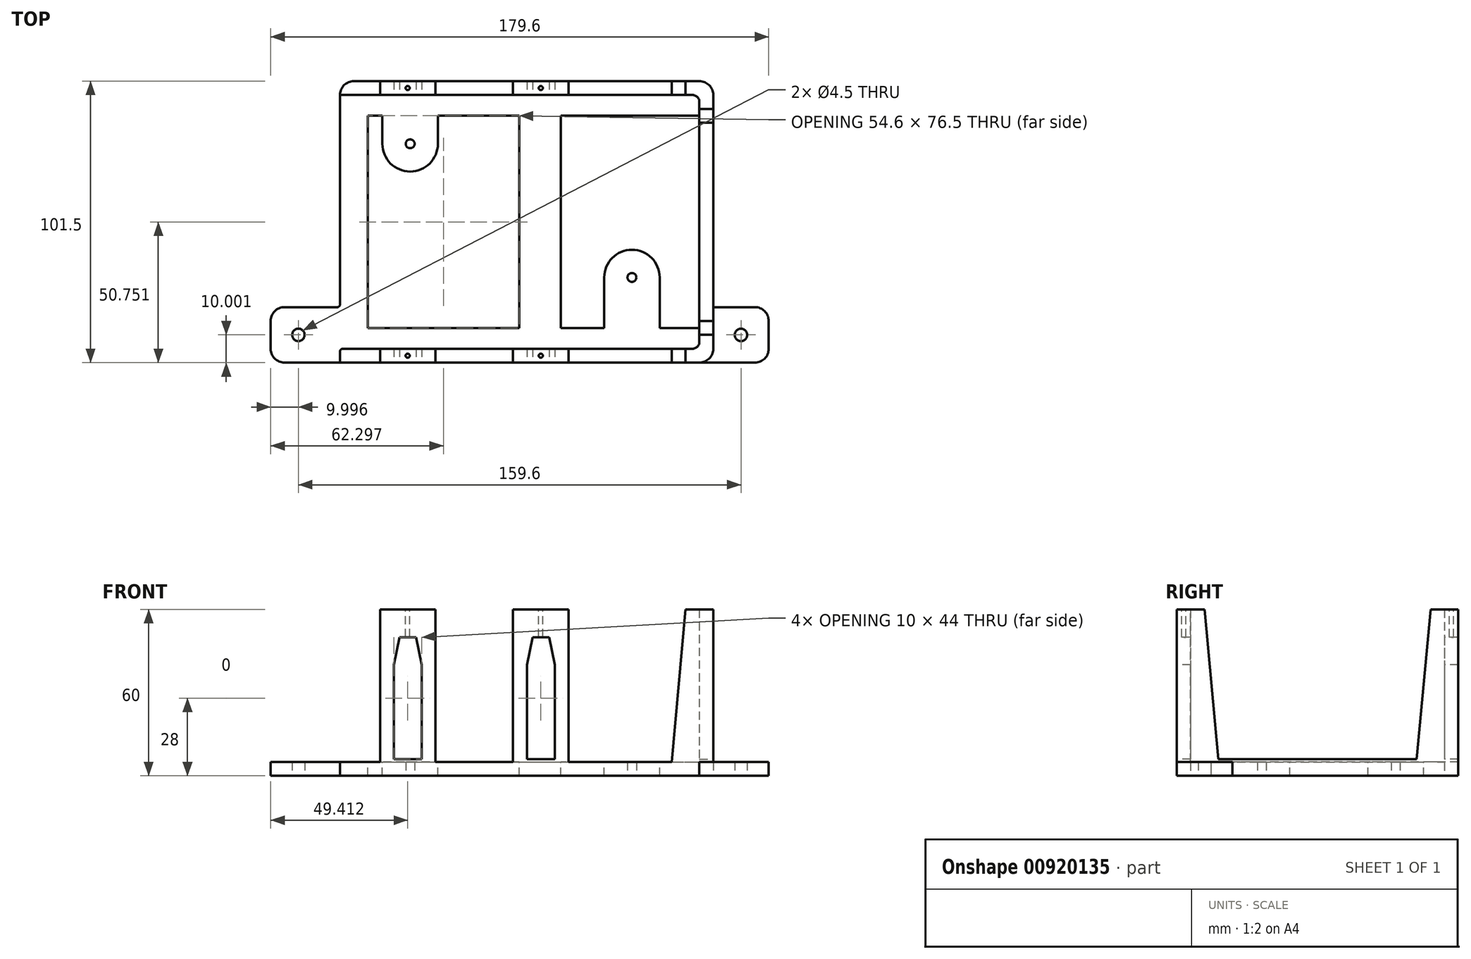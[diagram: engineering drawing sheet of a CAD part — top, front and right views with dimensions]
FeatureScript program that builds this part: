
annotation { "Feature Type Name" : "Feature", "Feature Type Description" : "" }
export const myFeature = defineFeature(function(context is Context, id is Id, definition is map)
    precondition{}
    {
        {
            var Q0;
            Q0=qCreatedBy(makeId("Top.planeOp"),FACE);
            var sketch = newSketch(context, id + "F0", { "sketchPlane" : qUnion([Q0])});
            skLineSegment(sketch, "E0.bottom", {"start": v(-74.7, 33.21) * mm, "end": v(26.9, 33.21) * mm, "construction": true});
            skLineSegment(sketch, "E0.top", {"start": v(-74.7, -20.09) * mm, "end": v(26.9, -20.09) * mm, "construction": true});
            skLineSegment(sketch, "E0.left", {"start": v(-74.7, 33.21) * mm, "end": v(-74.7, -20.09) * mm, "construction": true});
            skLineSegment(sketch, "E0.right", {"start": v(26.9, 33.21) * mm, "end": v(26.9, -20.09) * mm, "construction": true});
            skCircle(sketch, "E1", {"center": v(-60.7, -17.59) * mm, "radius": 1.6 * mm, "construction": true});
            skCircle(sketch, "E2", {"center": v(-59.4, 30.61) * mm, "radius": 1.6 * mm});
            skCircle(sketch, "E3", {"center": v(15.5, 30.61) * mm, "radius": 1.6 * mm, "construction": true});
            skCircle(sketch, "E4", {"center": v(20.58, -17.59) * mm, "radius": 1.6 * mm});
            skCircle(sketch, "E5", {"center": v(-8.6, -12.49) * mm, "radius": 1.6 * mm, "construction": true});
            skCircle(sketch, "E6", {"center": v(-8.6, 15.41) * mm, "radius": 1.6 * mm, "construction": true});
            skLineSegment(sketch, "E7.bottom", {"start": v(-79.7, 53.21) * mm, "end": v(44.9, 53.21) * mm});
            skLineSegment(sketch, "E7.top", {"start": v(-84.7, -48.29) * mm, "end": v(44.9, -48.29) * mm});
            skLineSegment(sketch, "E7.left", {"start": v(-50.13, 53.21) * mm, "end": v(-50.13, -48.29) * mm, "construction": true});
            skLineSegment(sketch, "E7.right", {"start": v(49.9, 48.21) * mm, "end": v(49.9, -43.29) * mm});
            skLineSegment(sketch, "E8.0", {"start": v(-83.7, -43.29) * mm, "end": v(42.4, -43.29) * mm});
            skLineSegment(sketch, "E8.1", {"start": v(44.9, 45.71) * mm, "end": v(44.9, -40.79) * mm});
            skLineSegment(sketch, "E8.2", {"start": v(-84.7, 48.21) * mm, "end": v(42.4, 48.21) * mm});
            skLineSegment(sketch, "E9", {"start": v(-84.7, 48.21) * mm, "end": v(-84.7, -27.29) * mm});
            skLineSegment(sketch, "E10", {"start": v(-104.7, -28.29) * mm, "end": v(-85.7, -28.29) * mm});
            skLineSegment(sketch, "E11", {"start": v(-109.7, -33.29) * mm, "end": v(-109.7, -43.29) * mm});
            skLineSegment(sketch, "E12", {"start": v(-104.7, -48.29) * mm, "end": v(-84.7, -48.29) * mm});
            skLineSegment(sketch, "E13", {"start": v(44.9, -48.29) * mm, "end": v(64.9, -48.29) * mm});
            skLineSegment(sketch, "E14", {"start": v(69.9, -43.29) * mm, "end": v(69.9, -33.29) * mm});
            skLineSegment(sketch, "E15.trimOffspring", {"start": v(49.9, -28.29) * mm, "end": v(64.9, -28.29) * mm});
            skLineSegment(sketch, "E16.trimOffspring", {"start": v(-84.7, -44.29) * mm, "end": v(-84.7, -48.29) * mm});
            skCircle(sketch, "E17", {"center": v(-99.7, -38.29) * mm, "radius": 2.25 * mm});
            skCircle(sketch, "E18", {"center": v(59.9, -38.29) * mm, "radius": 2.25 * mm});
            skPoint(sketch, "E19.visualSharp", {"position": v(44.9, 48.21) * mm});
            skArc(sketch, "E19.filletArc", {"start": v(44.9, 45.71) * mm, "mid": v(44.16, 47.48) * mm, "end": v(42.4, 48.21) * mm});
            skPoint(sketch, "E20.visualSharp", {"position": v(49.9, 53.21) * mm});
            skArc(sketch, "E20.filletArc", {"start": v(49.9, 48.21) * mm, "mid": v(48.43, 51.75) * mm, "end": v(44.9, 53.21) * mm});
            skPoint(sketch, "E21.visualSharp", {"position": v(44.9, -43.29) * mm});
            skArc(sketch, "E21.filletArc", {"start": v(42.4, -43.29) * mm, "mid": v(44.16, -42.56) * mm, "end": v(44.9, -40.79) * mm});
            skPoint(sketch, "E22.visualSharp", {"position": v(-109.7, -48.29) * mm});
            skArc(sketch, "E22.filletArc", {"start": v(-109.7, -43.29) * mm, "mid": v(-108.24, -46.82) * mm, "end": v(-104.7, -48.29) * mm});
            skPoint(sketch, "E23.visualSharp", {"position": v(-109.7, -28.29) * mm});
            skArc(sketch, "E23.filletArc", {"start": v(-104.7, -28.29) * mm, "mid": v(-108.24, -29.75) * mm, "end": v(-109.7, -33.29) * mm});
            skPoint(sketch, "E24.visualSharp", {"position": v(69.9, -28.29) * mm});
            skArc(sketch, "E24.filletArc", {"start": v(69.9, -33.29) * mm, "mid": v(68.43, -29.75) * mm, "end": v(64.9, -28.29) * mm});
            skPoint(sketch, "E25.visualSharp", {"position": v(69.9, -48.29) * mm});
            skArc(sketch, "E25.filletArc", {"start": v(64.9, -48.29) * mm, "mid": v(68.43, -46.82) * mm, "end": v(69.9, -43.29) * mm});
            skPoint(sketch, "E26.visualSharp", {"position": v(-84.7, 53.21) * mm});
            skArc(sketch, "E26.filletArc", {"start": v(-79.7, 53.21) * mm, "mid": v(-83.24, 51.75) * mm, "end": v(-84.7, 48.21) * mm});
            skPoint(sketch, "E27.visualSharp", {"position": v(-84.7, -28.29) * mm});
            skArc(sketch, "E27.filletArc", {"start": v(-85.7, -28.29) * mm, "mid": v(-85, -28) * mm, "end": v(-84.7, -27.29) * mm});
            skPoint(sketch, "E28.visualSharp", {"position": v(-84.7, -43.29) * mm});
            skArc(sketch, "E28.filletArc", {"start": v(-83.7, -43.29) * mm, "mid": v(-84.41, -43.58) * mm, "end": v(-84.7, -44.29) * mm});
            skPoint(sketch, "E29.visualSharp", {"position": v(49.9, -48.29) * mm});
            skArc(sketch, "E29.filletArc", {"start": v(44.9, -48.29) * mm, "mid": v(48.43, -46.82) * mm, "end": v(49.9, -43.29) * mm});
            skSolve(sketch);
        }
        {
            var Q0;
            Q0=makeQuery(id+"F0.imprint","IMPRINT",FACE,{"disambiguationData":[TD([[makeQuery(id+"F0.imprint","IMPRINT",EDGE,{"derivedFrom":sQuery(id+"F0.wireOp",EDGE,"E2")}),-1.0]])]});
            var Q1;
            {var subQ0=sQuery(id+"F0.wireOp",EDGE,"E13");Q1=makeQuery(id+"F0.imprint","IMPRINT",FACE,{"disambiguationData":[TD([[makeQuery(id+"F0.imprint","IMPRINT",EDGE,{"derivedFrom":subQ0}),1.0]])]});}
            extrude(context, id + "F1", {"entities" : qUnion([Q0, Q1]), "depth" : 5 * mm, "offsetDistance" : 25 * mm});
        }
        {
            var Q0;
            Q0=makeQuery(id+"F0.imprint","IMPRINT",FACE,{"disambiguationData":[TD([[makeQuery(id+"F0.imprint","IMPRINT",EDGE,{"derivedFrom":sQuery(id+"F0.wireOp",EDGE,"E7.bottom")}),-1.0]])]});
            extrude(context, id + "F2", {"entities" : qUnion([Q0]), "depth" : 60 * mm, "offsetDistance" : 25 * mm});
        }
        {
            var Q0;
            Q0=makeQuery(id+"F2.opExtrude","CAP_FACE",FACE,{"disambiguationData":[OSD([sQuery(id+"F0.wireOp",EDGE,"E7.bottom"),sQuery(id+"F0.wireOp",EDGE,"E7.top"),sQuery(id+"F0.wireOp",EDGE,"E7.right"),sQuery(id+"F0.wireOp",EDGE,"E8.0"),sQuery(id+"F0.wireOp",EDGE,"E8.1"),sQuery(id+"F0.wireOp",EDGE,"E8.2"),sQuery(id+"F0.wireOp",EDGE,"E16.trimOffspring"),sQuery(id+"F0.wireOp",EDGE,"E19.filletArc"),sQuery(id+"F0.wireOp",EDGE,"E20.filletArc"),sQuery(id+"F0.wireOp",EDGE,"E21.filletArc"),sQuery(id+"F0.wireOp",EDGE,"E26.filletArc"),sQuery(id+"F0.wireOp",EDGE,"E28.filletArc"),sQuery(id+"F0.wireOp",EDGE,"E29.filletArc")])],"isStart":false});
            var sketch = newSketch(context, id + "F3", { "sketchPlane" : qUnion([Q0])});
            skLineSegment(sketch, "E30", {"start": v(-88.25, 50.71) * mm, "end": v(116.83, 50.71) * mm, "construction": true});
            skLineSegment(sketch, "E31", {"start": v(-113.69, -45.79) * mm, "end": v(146.47, -45.79) * mm, "construction": true});
            skLineSegment(sketch, "E32.0", {"start": v(-83.7, -43.29) * mm, "end": v(42.4, -43.29) * mm});
            skLineSegment(sketch, "E33.0", {"start": v(-84.7, -48.29) * mm, "end": v(44.9, -48.29) * mm});
            skLineSegment(sketch, "E34.0", {"start": v(-84.7, 48.21) * mm, "end": v(42.4, 48.21) * mm});
            skLineSegment(sketch, "E35.0", {"start": v(-79.7, 53.21) * mm, "end": v(44.9, 53.21) * mm});
            skCircle(sketch, "E36", {"center": v(-60.29, 50.71) * mm, "radius": 0.75 * mm});
            skLineSegment(sketch, "E37", {"start": v(-60.29, 50.71) * mm, "end": v(-60.29, -65.98) * mm, "construction": true});
            skCircle(sketch, "E38", {"center": v(-60.29, -45.79) * mm, "radius": 0.75 * mm});
            skCircle(sketch, "E39", {"center": v(-12.29, -45.79) * mm, "radius": 0.75 * mm});
            skCircle(sketch, "E40", {"center": v(-12.29, 50.71) * mm, "radius": 0.75 * mm});
            skSolve(sketch);
        }
        {
            var Q0;
            Q0=makeQuery(id+"F3.imprint","IMPRINT",FACE,{"disambiguationData":[TD([[makeQuery(id+"F3.imprint","IMPRINT",EDGE,{"derivedFrom":sQuery(id+"F3.wireOp",EDGE,"E40")}),1.0]])]});
            var Q1;
            Q1=makeQuery(id+"F3.imprint","IMPRINT",FACE,{"disambiguationData":[TD([[makeQuery(id+"F3.imprint","IMPRINT",EDGE,{"derivedFrom":sQuery(id+"F3.wireOp",EDGE,"E36")}),1.0]])]});
            var Q2;
            Q2=makeQuery(id+"F3.imprint","IMPRINT",FACE,{"disambiguationData":[TD([[makeQuery(id+"F3.imprint","IMPRINT",EDGE,{"derivedFrom":sQuery(id+"F3.wireOp",EDGE,"E38")}),1.0]])]});
            var Q3;
            Q3=makeQuery(id+"F3.imprint","IMPRINT",FACE,{"disambiguationData":[TD([[makeQuery(id+"F3.imprint","IMPRINT",EDGE,{"derivedFrom":sQuery(id+"F3.wireOp",EDGE,"E39")}),1.0]])]});
            extrude(context, id + "F4", {"entities" : qUnion([Q0, Q1, Q2, Q3]), "operationType" : NewBodyOperationType.REMOVE, "oppositeDirection" : true, "depth" : 20 * mm, "offsetDistance" : 25 * mm});
        }
        {
            var Q0;
            Q0=makeQuery(id+"F2.opExtrude","SWEPT_FACE",FACE,{"disambiguationData":[OSD([sQuery(id+"F0.wireOp",EDGE,"E7.right")])]});
            var sketch = newSketch(context, id + "F5", { "sketchPlane" : qUnion([Q0])});
            skLineSegment(sketch, "E41.0", {"start": v(-28.29, 5) * mm, "end": v(-43.29, 5) * mm});
            skLineSegment(sketch, "E42.0", {"start": v(-43.29, 60) * mm, "end": v(-43.29, 0) * mm});
            skLineSegment(sketch, "E43", {"start": v(-38.29, 60) * mm, "end": v(-33.29, 6) * mm});
            skLineSegment(sketch, "E44", {"start": v(-33.29, 6) * mm, "end": v(38.21, 6) * mm});
            skLineSegment(sketch, "E45", {"start": v(38.21, 6) * mm, "end": v(43.21, 60) * mm});
            skLineSegment(sketch, "E46", {"start": v(-43.29, 60) * mm, "end": v(-38.29, 60) * mm});
            skLineSegment(sketch, "E47", {"start": v(48.21, 60) * mm, "end": v(43.21, 60) * mm});
            skSolve(sketch);
        }
        {
            var Q0;
            {var subQ0=sQuery(id+"F5.wireOp",EDGE,"E43");Q0=makeQuery(id+"F5.imprint","IMPRINT",FACE,{"disambiguationData":[TD([[makeQuery(id+"F5.imprint","IMPRINT",EDGE,{"derivedFrom":subQ0}),1.0]])]});}
            extrude(context, id + "F6", {"entities" : qUnion([Q0]), "operationType" : NewBodyOperationType.REMOVE, "oppositeDirection" : true, "depth" : 25 * mm, "offsetDistance" : 25 * mm});
        }
        {
            var Q0;
            Q0=makeQuery(id+"F2.opExtrude","SWEPT_FACE",FACE,{"disambiguationData":[OSD([sQuery(id+"F0.wireOp",EDGE,"E7.top")])]});
            var sketch = newSketch(context, id + "F7", { "sketchPlane" : qUnion([Q0])});
            skSolve(sketch);
        }
        {
            var Q0;
            {var subQ0=sQuery(id+"F0.wireOp",EDGE,"E28.filletArc");var subQ1=sQuery(id+"F0.wireOp",EDGE,"E21.filletArc");var subQ2=sQuery(id+"F0.wireOp",EDGE,"E16.trimOffspring");var subQ3=sQuery(id+"F0.wireOp",EDGE,"E29.filletArc");var subQ4=sQuery(id+"F0.wireOp",EDGE,"E7.top");var subQ5=sQuery(id+"F0.wireOp",EDGE,"E7.right");var subQ6=sQuery(id+"F0.wireOp",EDGE,"E8.0");var subQ7=sQuery(id+"F0.wireOp",EDGE,"E8.1");Q0=makeQuery(id+"F6.boolean.opBoolean","SPLIT",FACE,{"disambiguationData":[TD([makeQuery(id+"F2.opExtrude","SWEPT_FACE",FACE,{"disambiguationData":[OSD([subQ4])]})])],"derivedFrom":makeQuery(id+"F2.opExtrude","CAP_FACE",FACE,{"disambiguationData":[OSD([sQuery(id+"F0.wireOp",EDGE,"E7.bottom"),subQ4,subQ5,subQ6,subQ7,sQuery(id+"F0.wireOp",EDGE,"E8.2"),subQ2,sQuery(id+"F0.wireOp",EDGE,"E19.filletArc"),sQuery(id+"F0.wireOp",EDGE,"E20.filletArc"),subQ1,sQuery(id+"F0.wireOp",EDGE,"E26.filletArc"),subQ0,subQ3])],"isStart":false})});}
            var sketch = newSketch(context, id + "F8", { "sketchPlane" : qUnion([Q0])});
            skLineSegment(sketch, "E48", {"start": v(-70.29, -43.29) * mm, "end": v(-70.29, -48.29) * mm});
            skLineSegment(sketch, "E49", {"start": v(-50.29, -43.29) * mm, "end": v(-50.29, -48.29) * mm});
            skLineSegment(sketch, "E50", {"start": v(-22.29, -43.29) * mm, "end": v(-22.29, -48.29) * mm});
            skLineSegment(sketch, "E51", {"start": v(-2.29, -43.29) * mm, "end": v(-2.29, -48.29) * mm});
            skCircle(sketch, "E52.0", {"center": v(-60.29, -45.79) * mm, "radius": 0.75 * mm});
            skCircle(sketch, "E53.0", {"center": v(-12.29, -45.79) * mm, "radius": 0.75 * mm});
            skSolve(sketch);
        }
        {
            var Q0;
            {var subQ0=sQuery(id+"F0.wireOp",EDGE,"E7.top");Q0=makeQuery(id+"F7.imprint","IMPRINT",FACE,{"disambiguationData":[TD([[makeQuery(id+"F7.imprint","IMPRINT",EDGE,{"derivedFrom":makeQuery(id+"F2.opExtrude","CAP_EDGE",EDGE,{"disambiguationData":[OSD([subQ0])],"isStart":true})}),1.0]])]});}
            var sketch = newSketch(context, id + "F9", { "sketchPlane" : qUnion([Q0])});
            skPoint(sketch, "E54.0", {"position": v(-70.29, 60) * mm});
            skPoint(sketch, "E54.1", {"position": v(-50.29, 60) * mm});
            skPoint(sketch, "E55.0", {"position": v(-22.29, 60) * mm});
            skPoint(sketch, "E55.1", {"position": v(-2.29, 60) * mm});
            skPoint(sketch, "E56.0", {"position": v(44.9, 5) * mm});
            skLineSegment(sketch, "E57", {"start": v(44.9, 5) * mm, "end": v(-84.7, 5) * mm});
            skLineSegment(sketch, "E58", {"start": v(-50.29, 60) * mm, "end": v(-50.29, 5) * mm});
            skLineSegment(sketch, "E59", {"start": v(-70.29, 60) * mm, "end": v(-70.29, 5) * mm});
            skLineSegment(sketch, "E60", {"start": v(-22.29, 60) * mm, "end": v(-22.29, 5) * mm});
            skPoint(sketch, "E60.endSnap0", {"position": v(-19.11, 5) * mm});
            skLineSegment(sketch, "E61", {"start": v(-2.29, 60) * mm, "end": v(-2.29, 5) * mm});
            skLineSegment(sketch, "E62.0", {"start": v(-84.7, 60) * mm, "end": v(44.9, 60) * mm});
            skLineSegment(sketch, "E63", {"start": v(34.9, 5) * mm, "end": v(39.9, 60) * mm});
            skPoint(sketch, "E64.0", {"position": v(-84.7, 5) * mm});
            skPoint(sketch, "E65.orphan", {"position": v(-83.12, 5) * mm});
            skLineSegment(sketch, "E66", {"start": v(-70.29, 60) * mm, "end": v(-50.29, 60) * mm, "construction": true});
            skLineSegment(sketch, "E67", {"start": v(-22.29, 60) * mm, "end": v(-2.29, 60) * mm, "construction": true});
            skLineSegment(sketch, "E68", {"start": v(-60.29, 60) * mm, "end": v(-60.29, 19.22) * mm, "construction": true});
            skLineSegment(sketch, "E69", {"start": v(-12.29, 60) * mm, "end": v(-12.29, 10.63) * mm, "construction": true});
            skLineSegment(sketch, "E70", {"start": v(-65.29, 50) * mm, "end": v(-55.29, 50) * mm});
            skLineSegment(sketch, "E71", {"start": v(-65.29, 6) * mm, "end": v(-55.29, 6) * mm});
            skLineSegment(sketch, "E72", {"start": v(-65.29, 6) * mm, "end": v(-65.29, 50) * mm});
            skLineSegment(sketch, "E73", {"start": v(-55.29, 6) * mm, "end": v(-55.29, 50) * mm});
            skLineSegment(sketch, "E74", {"start": v(-17.29, 6) * mm, "end": v(-17.29, 50) * mm});
            skLineSegment(sketch, "E75", {"start": v(-7.29, 6) * mm, "end": v(-7.29, 50) * mm});
            skPoint(sketch, "E76.orphan", {"position": v(-81.61, 6) * mm});
            skPoint(sketch, "E77.orphan", {"position": v(-81.8, 50) * mm});
            skLineSegment(sketch, "E78.trimOffspring", {"start": v(-17.29, 6) * mm, "end": v(-7.29, 6) * mm});
            skLineSegment(sketch, "E79.trimOffspring", {"start": v(-17.29, 50) * mm, "end": v(-7.29, 50) * mm});
            skLineSegment(sketch, "E80", {"start": v(-65.29, 40) * mm, "end": v(-63.29, 50) * mm});
            skLineSegment(sketch, "E81", {"start": v(-55.29, 40) * mm, "end": v(-57.29, 50) * mm});
            skLineSegment(sketch, "E82", {"start": v(-17.29, 40) * mm, "end": v(-15.29, 50) * mm});
            skLineSegment(sketch, "E83", {"start": v(-9.29, 50) * mm, "end": v(-7.29, 40) * mm});
            skSolve(sketch);
        }
        {
            var Q0;
            {var subQ0=sQuery(id+"F9.wireOp",EDGE,"E58");Q0=makeQuery(id+"F9.imprint","IMPRINT",FACE,{"disambiguationData":[TD([[makeQuery(id+"F9.imprint","IMPRINT",EDGE,{"derivedFrom":subQ0}),1.0]])]});}
            var Q1;
            {var subQ0=sQuery(id+"F9.wireOp",EDGE,"E61");Q1=makeQuery(id+"F9.imprint","IMPRINT",FACE,{"disambiguationData":[TD([[makeQuery(id+"F9.imprint","IMPRINT",EDGE,{"derivedFrom":subQ0}),1.0]])]});}
            extrude(context, id + "F10", {"entities" : qUnion([Q0, Q1]), "operationType" : NewBodyOperationType.REMOVE, "oppositeDirection" : true, "depth" : 200 * mm, "offsetDistance" : 25 * mm});
        }
        {
            var Q0;
            {var subQ0=sQuery(id+"F0.wireOp",EDGE,"E7.top");Q0=makeQuery(id+"F7.imprint","IMPRINT",FACE,{"disambiguationData":[TD([[makeQuery(id+"F7.imprint","IMPRINT",EDGE,{"derivedFrom":makeQuery(id+"F2.opExtrude","CAP_EDGE",EDGE,{"disambiguationData":[OSD([subQ0])],"isStart":true})}),1.0]])]});}
            var sketch = newSketch(context, id + "F11", { "sketchPlane" : qUnion([Q0])});
            skPoint(sketch, "E84.0", {"position": v(-84.7, 5) * mm});
            skPoint(sketch, "E85.0", {"position": v(-70.29, 60) * mm});
            skLineSegment(sketch, "E86", {"start": v(-84.7, 5) * mm, "end": v(-70.29, 60) * mm});
            skPoint(sketch, "E87.0", {"position": v(-84.7, 60) * mm});
            skLineSegment(sketch, "E88", {"start": v(-84.7, 60) * mm, "end": v(-70.29, 60) * mm});
            skLineSegment(sketch, "E89", {"start": v(-84.7, 60) * mm, "end": v(-84.7, 5) * mm});
            skSolve(sketch);
        }
        {
            var Q0;
            Q0=makeQuery(id+"F11.imprint","IMPRINT",FACE,{"disambiguationData":[TD([[makeQuery(id+"F11.imprint","IMPRINT",EDGE,{"derivedFrom":sQuery(id+"F11.wireOp",EDGE,"E86")}),1.0]])]});
            extrude(context, id + "F12", {"entities" : qUnion([Q0]), "operationType" : NewBodyOperationType.REMOVE, "oppositeDirection" : true, "depth" : 200 * mm, "offsetDistance" : 25 * mm});
        }
        {
            var Q0;
            {var subQ1=sQuery(id+"F9.wireOp",EDGE,"E71");Q0=makeQuery(id+"F9.imprint","IMPRINT",FACE,{"disambiguationData":[TD([[makeQuery(id+"F9.imprint","IMPRINT",EDGE,{"derivedFrom":subQ1}),1.0]])]});}
            var Q1;
            {var subQ3=sQuery(id+"F9.wireOp",EDGE,"E78.trimOffspring");Q1=makeQuery(id+"F9.imprint","IMPRINT",FACE,{"disambiguationData":[TD([[makeQuery(id+"F9.imprint","IMPRINT",EDGE,{"derivedFrom":subQ3}),1.0]])]});}
            extrude(context, id + "F13", {"entities" : qUnion([Q0, Q1]), "operationType" : NewBodyOperationType.REMOVE, "oppositeDirection" : true, "depth" : 200 * mm, "offsetDistance" : 25 * mm});
        }
        {
            var Q0;
            Q0=makeQuery(id+"F1.opExtrude","CAP_FACE",FACE,{"disambiguationData":[OSD([sQuery(id+"F0.wireOp",EDGE,"E2"),sQuery(id+"F0.wireOp",EDGE,"E4"),sQuery(id+"F0.wireOp",EDGE,"E8.0"),sQuery(id+"F0.wireOp",EDGE,"E8.1"),sQuery(id+"F0.wireOp",EDGE,"E8.2"),sQuery(id+"F0.wireOp",EDGE,"E9"),sQuery(id+"F0.wireOp",EDGE,"E10"),sQuery(id+"F0.wireOp",EDGE,"E11"),sQuery(id+"F0.wireOp",EDGE,"E12"),sQuery(id+"F0.wireOp",EDGE,"E16.trimOffspring"),sQuery(id+"F0.wireOp",EDGE,"E17"),sQuery(id+"F0.wireOp",EDGE,"E19.filletArc"),sQuery(id+"F0.wireOp",EDGE,"E21.filletArc"),sQuery(id+"F0.wireOp",EDGE,"E22.filletArc"),sQuery(id+"F0.wireOp",EDGE,"E23.filletArc"),sQuery(id+"F0.wireOp",EDGE,"E27.filletArc"),sQuery(id+"F0.wireOp",EDGE,"E28.filletArc")])],"isStart":false});
            var sketch = newSketch(context, id + "F14", { "sketchPlane" : qUnion([Q0])});
            skArc(sketch, "E90", {"start": v(-69.4, 30.61) * mm, "mid": v(-59.4, 20.61) * mm, "end": v(-49.4, 30.61) * mm});
            skArc(sketch, "E91", {"start": v(30.58, -17.59) * mm, "mid": v(20.58, -7.59) * mm, "end": v(10.58, -17.59) * mm});
            skLineSegment(sketch, "E92", {"start": v(-69.4, 30.61) * mm, "end": v(-69.4, 48.21) * mm});
            skLineSegment(sketch, "E93.0", {"start": v(-84.7, 48.21) * mm, "end": v(42.4, 48.21) * mm});
            skLineSegment(sketch, "E94", {"start": v(-49.4, 30.61) * mm, "end": v(-49.4, 48.21) * mm});
            skLineSegment(sketch, "E95.0", {"start": v(-83.7, -43.29) * mm, "end": v(42.4, -43.29) * mm});
            skLineSegment(sketch, "E96", {"start": v(-74.7, 48.21) * mm, "end": v(-74.7, -43.29) * mm});
            skLineSegment(sketch, "E97", {"start": v(10.58, -17.59) * mm, "end": v(10.58, -43.29) * mm});
            skLineSegment(sketch, "E98", {"start": v(30.58, -17.59) * mm, "end": v(30.58, -43.29) * mm});
            skLineSegment(sketch, "E99.bottom", {"start": v(-5.1, -43.29) * mm, "end": v(-20.1, -43.29) * mm});
            skLineSegment(sketch, "E99.top", {"start": v(-5.1, 48.21) * mm, "end": v(-20.1, 48.21) * mm});
            skLineSegment(sketch, "E99.left", {"start": v(-5.1, -43.29) * mm, "end": v(-5.1, 48.21) * mm});
            skLineSegment(sketch, "E99.right", {"start": v(-20.1, -43.29) * mm, "end": v(-20.1, 48.21) * mm});
            skLineSegment(sketch, "E100", {"start": v(30.58, -35.79) * mm, "end": v(44.9, -35.79) * mm});
            skLineSegment(sketch, "E101", {"start": v(10.58, -35.79) * mm, "end": v(-5.1, -35.79) * mm});
            skLineSegment(sketch, "E102", {"start": v(-20.1, -35.79) * mm, "end": v(-74.7, -35.79) * mm});
            skLineSegment(sketch, "E103", {"start": v(-74.7, 40.71) * mm, "end": v(-69.4, 40.71) * mm});
            skLineSegment(sketch, "E104", {"start": v(-49.4, 40.71) * mm, "end": v(-20.1, 40.71) * mm});
            skLineSegment(sketch, "E105", {"start": v(-5.1, 40.71) * mm, "end": v(44.9, 40.71) * mm});
            skSolve(sketch);
        }
        {
            var Q0;
            Q0=makeQuery(id+"F14.imprint","IMPRINT",FACE,{"disambiguationData":[TD([[makeQuery(id+"F14.imprint","IMPRINT",EDGE,{"derivedFrom":sQuery(id+"F14.wireOp",EDGE,"E90")}),-1.0]])]});
            var Q1;
            Q1=makeQuery(id+"F14.imprint","IMPRINT",FACE,{"disambiguationData":[TD([[makeQuery(id+"F14.imprint","IMPRINT",EDGE,{"derivedFrom":sQuery(id+"F14.wireOp",EDGE,"E91")}),-1.0]])]});
            extrude(context, id + "F15", {"entities" : qUnion([Q0, Q1]), "operationType" : NewBodyOperationType.REMOVE, "oppositeDirection" : true, "depth" : 100 * mm, "offsetDistance" : 25 * mm});
        }
        {
            var Q0;
            {var subQ3=sQuery(id+"F9.wireOp",EDGE,"E59");Q0=makeQuery(id+"F9.imprint","IMPRINT",FACE,{"disambiguationData":[TD([[makeQuery(id+"F9.imprint","IMPRINT",EDGE,{"derivedFrom":subQ3}),-1.0]])]});}
            extrude(context, id + "F16", {"entities" : qUnion([Q0]), "operationType" : NewBodyOperationType.REMOVE, "oppositeDirection" : true, "depth" : 222 * mm, "offsetDistance" : 25 * mm});
        }
    });
